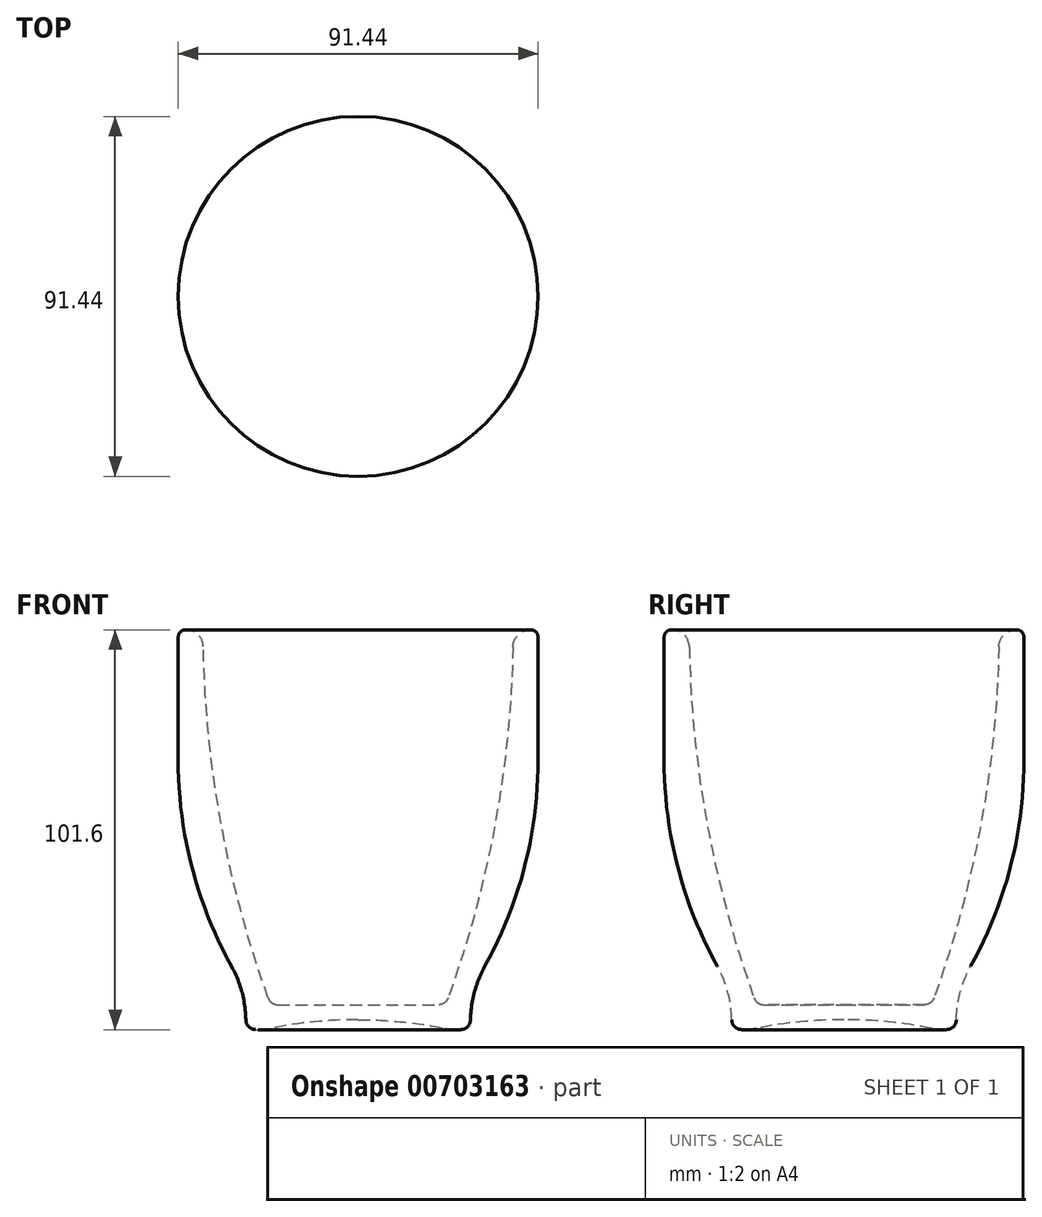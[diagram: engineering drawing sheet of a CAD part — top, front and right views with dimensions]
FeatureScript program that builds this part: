
annotation { "Feature Type Name" : "Feature", "Feature Type Description" : "" }
export const myFeature = defineFeature(function(context is Context, id is Id, definition is map)
    precondition{}
    {
        {
            var Q0;
            Q0=qCreatedBy(makeId("Front.planeOp"),FACE);
            var sketch = newSketch(context, id + "F0", { "sketchPlane" : qUnion([Q0])});
            skLineSegment(sketch, "E0", {"start": v(0, 0) * mm, "end": v(20.45, 0) * mm});
            skLineSegment(sketch, "E1.bottom", {"start": v(0, -6.35) * mm, "end": v(45.72, -6.35) * mm, "construction": true});
            skLineSegment(sketch, "E1.left", {"start": v(0, -6.35) * mm, "end": v(0, 95.25) * mm, "construction": true});
            skArc(sketch, "E2", {"start": v(22.84, 1.68) * mm, "mid": v(34.72, 45.61) * mm, "end": v(39.32, 90.9) * mm});
            skArc(sketch, "E3", {"start": v(22.23, -6.03) * mm, "mid": v(11.17, -4.37) * mm, "end": v(0, -3.8) * mm});
            skLineSegment(sketch, "E4", {"start": v(22.23, 0) * mm, "end": v(22.23, -6.35) * mm, "construction": true});
            skLineSegment(sketch, "E5", {"start": v(0, -3.8) * mm, "end": v(-5.14, -3.8) * mm, "construction": true});
            skArc(sketch, "E6", {"start": v(22.22, -6.03) * mm, "mid": v(24.15, -6.3) * mm, "end": v(26.1, -6.33) * mm});
            skLineSegment(sketch, "E7", {"start": v(25.4, -6.35) * mm, "end": v(25.4, -6.35) * mm});
            skLineSegment(sketch, "E8", {"start": v(45.72, 93.35) * mm, "end": v(45.72, 62.2) * mm});
            skArc(sketch, "E9", {"start": v(32.15, 9.68) * mm, "mid": v(42.27, 35.08) * mm, "end": v(45.72, 62.2) * mm});
            skArc(sketch, "E10", {"start": v(32.15, 9.68) * mm, "mid": v(29.51, 3.14) * mm, "end": v(28.53, -3.84) * mm});
            skLineSegment(sketch, "E11", {"start": v(0, -3.8) * mm, "end": v(0, 0) * mm});
            skLineSegment(sketch, "E12", {"start": v(43.82, 95.25) * mm, "end": v(43.76, 95.25) * mm});
            skPoint(sketch, "E13.visualSharp", {"position": v(39.37, 95.25) * mm});
            skArc(sketch, "E13.filletArc", {"start": v(43.76, 95.25) * mm, "mid": v(40.65, 93.98) * mm, "end": v(39.32, 90.9) * mm});
            skPoint(sketch, "E14.visualSharp", {"position": v(45.72, 95.25) * mm});
            skArc(sketch, "E14.filletArc", {"start": v(45.72, 93.35) * mm, "mid": v(45.16, 94.7) * mm, "end": v(43.82, 95.25) * mm});
            skPoint(sketch, "E15.visualSharp", {"position": v(22.23, 0) * mm});
            skArc(sketch, "E15.filletArc", {"start": v(20.45, 0) * mm, "mid": v(21.9, 0.46) * mm, "end": v(22.84, 1.68) * mm});
            skPoint(sketch, "E16.visualSharp", {"position": v(28.58, -6.03) * mm});
            skArc(sketch, "E16.filletArc", {"start": v(26.1, -6.33) * mm, "mid": v(27.81, -5.57) * mm, "end": v(28.53, -3.84) * mm});
            skSolve(sketch);
        }
        {
            var Q0;
            Q0=makeQuery(id+"F0.imprint","IMPRINT",FACE,{"disambiguationData":[TD([[makeQuery(id+"F0.imprint","IMPRINT",EDGE,{"derivedFrom":sQuery(id+"F0.wireOp",EDGE,"E0")}),-1.0]])]});
            var Q1;
            Q1=sQuery(id+"F0.wireOp",EDGE,"E1.left");
            revolve(context, id + "F1", {"surfaceOperationType" : NewSurfaceOperationType.NEW, "entities" : qUnion([Q0]), "axis" : qUnion([Q1]), "revolveType" : RevolveType.FULL});
        }
    });
